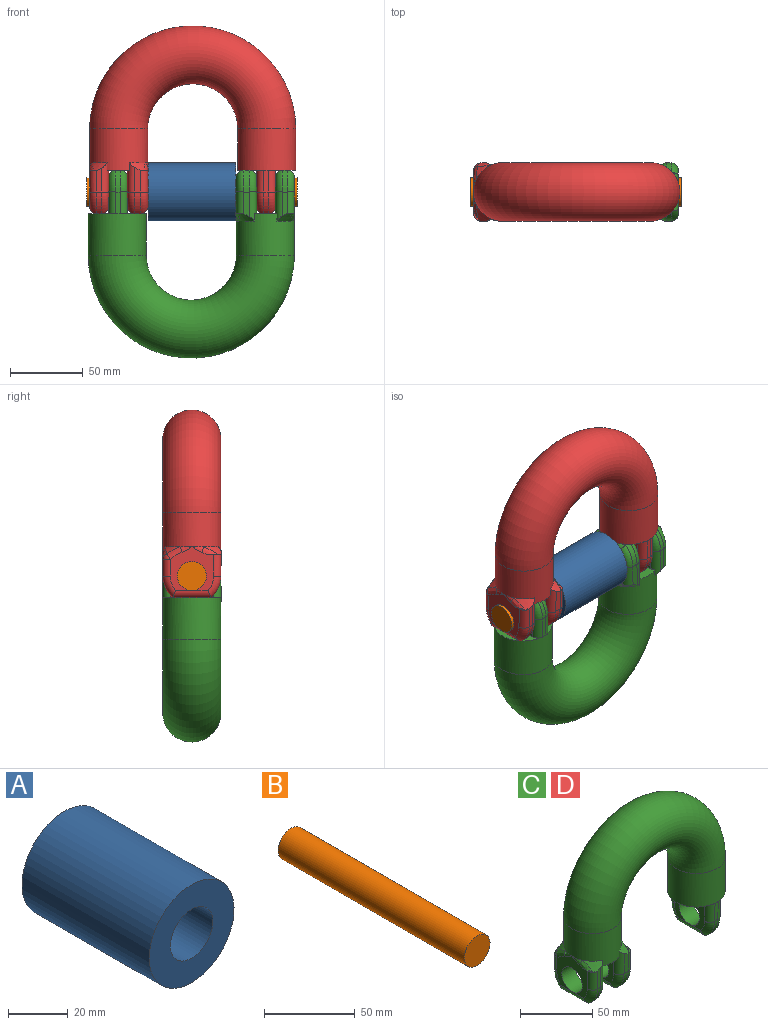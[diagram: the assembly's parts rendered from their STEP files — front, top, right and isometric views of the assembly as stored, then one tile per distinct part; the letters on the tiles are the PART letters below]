
ASSEMBLY  parts=4 mates=3
PART A: 4 faces, bbox 40x60x40 mm
  f0: cylinder r=10mm len=60mm, axis (0,1,0), area 3769.9mm2, adj f2,f3
  f1: cylinder r=20mm len=60mm, axis (0,1,0), area 7539.8mm2, adj f2,f3
  f2: plane 40x40mm, normal (0,-1,0), area 942.5mm2, adj f0,f1
  f3: plane 40x40mm, normal (0,1,0), area 942.5mm2, adj f0,f1
PART B: 3 faces, bbox 20x145x20 mm
  f0: cylinder r=10mm len=145mm, axis (0,1,0), area 9110.6mm2, adj f1,f2
  f1: plane 20x20mm, normal (0,-1,0), area 314.2mm2, adj f0
  f2: plane 20x20mm, normal (0,1,0), area 314.2mm2, adj f0
PART C: 86 faces, bbox 154.5x47.3x137.4 mm
  f0: plane 26.46x3mm, normal (0,0,-1), area 79.4mm2, adj f36,f37,f51,f52
  f1: plane 10.98x5.8mm, normal (0,0,1), area 8.1mm2, adj f10,f42,f63,f85
  f2: plane 24.41x4mm, normal (0,0,-1), area 97.6mm2, adj f29,f65,f69,f70
  f3: plane 7.38x0.67mm, normal (0,0,1), area 1.4mm2, adj f18,f26,f74,f79
  f4: plane 1.99x0.1mm, normal (0,0,1), area 0mm2, adj f18,f27,f76
  f5: plane 26.46x2.99mm, normal (0,0,-1), area 79.1mm2, adj f24,f28,f77,f82
  f6: plane 11.14x6.01mm, normal (0,0,1), area 9mm2, adj f8,f34,f40,f44,f48
  f7: plane 30.16x25mm, normal (1,0,0), area 413mm2, adj f14,f23,f47,f49,f51,f53,f55
  f8: plane 31x30.84mm, normal (-1,0,0), area 452.1mm2, adj f6,f23,f43,f44,f48,f50,f52,f54
  f9: plane 30.16x25mm, normal (-1,0,0), area 413mm2, adj f14,f22,f64,f67,f69,f72,f73
  f10: plane 31x30.84mm, normal (1,0,0), area 460.3mm2, adj f1,f19,f22,f45,f46,f61,f62,f63
  f11: plane 30.16x25mm, normal (1,0,0), area 413mm2, adj f15,f21,f74,f75,f76,f77,f78
  f12: plane 30.16x25mm, normal (-1,0,0), area 413mm2, adj f13,f21,f79,f80,f81,f82,f83
  f13: plane 39.11x16.08mm, normal (0,0,-1), area 359.5mm2, adj f12,f18,f79,f81
  f14: plane 40x15.68mm, normal (0,0,-1), area 517.2mm2, adj f7,f9,f16,f47,f55,f64,f73
  f15: plane 39.7x18.02mm, normal (0,0,-1), area 398.6mm2, adj f11,f18,f74,f76
  f16: cylinder r=20mm len=40mm, axis (0,0,1), area 3112.9mm2, adj f14,f17,f39,f40,f41,f42,f43,f46
  f17: torus R=51mm, axis (0,-1,0), area 20134mm2, adj f16,f18
  f18: cylinder r=20mm len=40mm, axis (0,0,-1), area 3581.4mm2, adj f3,f4,f13,f15,f17,f20
  f19: plane 11.13x6.01mm, normal (0,0,1), area 9mm2, adj f10,f31,f41,f45,f61
  f20: plane 3.92x0.39mm, normal (0,0,1), area 0.3mm2, adj f18,f27,f81
  f21: cylinder r=10mm len=20mm, axis (-1,0,0), area 816.3mm2, adj f11,f12
  f22: cylinder r=10mm len=20mm, axis (-1,0,0), area 879.6mm2, adj f9,f10
  f23: cylinder r=10mm len=20mm, axis (-1,0,0), area 816.8mm2, adj f7,f8
  f24: cylinder r=20mm len=15mm, axis (-1,0,0), area 50.8mm2, adj f5,f25,f74,f75,f79,f80
  f25: plane 3.2x0mm, normal (0,0,-1), area 0mm2, adj f24,f26,f74,f79
  f26: plane 15x2.99mm, normal (0,-1,-0.01), area 44.9mm2, adj f3,f25,f74,f79
  f27: plane 15x2.99mm, normal (0,1,0), area 44.9mm2, adj f4,f20,f28,f76,f81
  f28: cylinder r=20mm len=15mm, axis (-1,0,0), area 50.7mm2, adj f5,f27,f78,f83
  f29: cylinder r=20mm len=15mm, axis (-1,0,0), area 67.9mm2, adj f2,f30,f61,f62,f64,f67
  f30: plane 4.21x0mm, normal (0,0,-1), area 0mm2, adj f29,f31,f61,f64
  f31: plane 17.22x4.21mm, normal (0,-1,-0.01), area 64mm2, adj f19,f30,f41,f61,f64
  f32: plane 17.41x4.23mm, normal (0,1,0), area 64.5mm2, adj f33,f42,f63,f73
  f33: cylinder r=20mm len=13.33mm, axis (-1,0,0), area 58.4mm2, adj f32,f66,f70,f72
  f34: plane 16.64x3.11mm, normal (0,-1,-0.01), area 47.2mm2, adj f6,f35,f40,f47,f48
  f35: plane 3.21x0mm, normal (0,0,-1), area 0mm2, adj f34,f36,f47,f48
  f36: cylinder r=20mm len=15mm, axis (-1,0,0), area 50.9mm2, adj f0,f35,f47,f48,f49,f50
  f37: cylinder r=20mm len=15mm, axis (-1,0,0), area 50.9mm2, adj f0,f38,f53,f54
  f38: plane 13.72x3.01mm, normal (0,1,0), area 38.2mm2, adj f37,f55,f56,f57
  f39: cone r=25mm half-angle=45deg, axis (0,0,-1), area 52.2mm2, adj f16,f57,f59
  f40: cone r=25mm half-angle=45deg, axis (0,0,-1), area 70mm2, adj f6,f16,f34,f44,f47
  f41: cone r=25mm half-angle=45deg, axis (0,0,-1), area 73.1mm2, adj f16,f19,f31,f45,f64
  f42: cone r=25mm half-angle=45deg, axis (0,0,-1), area 71.4mm2, adj f1,f16,f32,f73,f85
  f43: bspline ~9.51x4.04mm, area 10.7mm2, adj f8,f16,f44
  f44: bspline ~13.39x9.91mm, area 33.3mm2, adj f6,f8,f40,f43
  f45: bspline ~13.39x9.91mm, area 33.3mm2, adj f10,f19,f41,f46
  f46: bspline ~9.51x4.04mm, area 10.7mm2, adj f10,f16,f45
  f47: cylinder r=5mm len=20.24mm, axis (0,0.01,-1), area 133.2mm2, adj f7,f14,f16,f34,f35,f36,f40,f49
  f48: cylinder r=5mm len=15.26mm, axis (0,0.01,-1), area 119.3mm2, adj f6,f8,f34,f35,f36,f50
  f49: torus R=15mm, axis (-1,0,0), area 111.6mm2, adj f7,f36,f47,f51
  f50: torus R=15mm, axis (1,0,0), area 111.6mm2, adj f8,f36,f48,f52
  f51: cylinder r=5mm len=26.46mm, axis (0,-1,0), area 191.7mm2, adj f0,f7,f49,f53
  f52: cylinder r=5mm len=26.46mm, axis (0,-1,0), area 191.7mm2, adj f0,f8,f50,f54
  f53: torus R=15mm, axis (-1,0,0), area 113.1mm2, adj f7,f37,f51,f55
  f54: torus R=15mm, axis (1,0,0), area 113.1mm2, adj f8,f37,f52,f56
  f55: cylinder r=5mm len=20mm, axis (0,0,1), area 125.9mm2, adj f7,f14,f16,f38,f53,f57
  f56: cylinder r=5mm len=11.72mm, axis (0,0,1), area 92mm2, adj f8,f38,f54,f58
  f57: bspline ~14.17x10.45mm, area 36.5mm2, adj f16,f38,f39,f55,f58
  f58: sphere r=5mm, area 14.6mm2, adj f56,f57,f59
  f59: bspline ~13.39x9.91mm, area 48.1mm2, adj f8,f39,f58,f60
  f60: bspline ~9.51x4.04mm, area 10.7mm2, adj f8,f16,f59
  f61: cylinder r=5mm len=15.26mm, axis (0,0.01,-1), area 119.3mm2, adj f10,f19,f29,f30,f31,f62
  f62: torus R=15mm, axis (1,0,0), area 111.6mm2, adj f10,f29,f61,f65
  f63: cylinder r=5mm len=15mm, axis (0,0,1), area 117.8mm2, adj f1,f10,f32,f66
  f64: cylinder r=5mm len=20.25mm, axis (0,-0.01,1), area 133mm2, adj f9,f14,f16,f29,f30,f31,f41,f67
  f65: cylinder r=5mm len=24.41mm, axis (0,-1,0), area 183.7mm2, adj f2,f10,f62,f68
  f66: torus R=15mm, axis (1,0,0), area 104.2mm2, adj f10,f33,f63,f68
  f67: torus R=15mm, axis (-1,0,0), area 111.6mm2, adj f9,f29,f64,f69
  f68: sphere r=5mm, area 16.6mm2, adj f65,f66,f70
  f69: cylinder r=5mm len=24.41mm, axis (0,-1,0), area 183.7mm2, adj f2,f9,f67,f71
  f70: cylinder r=5mm len=4mm, axis (-1,0,0), area 16.8mm2, adj f2,f33,f68,f71
  f71: sphere r=5mm, area 30mm2, adj f69,f70,f72
  f72: torus R=15mm, axis (-1,0,0), area 104.2mm2, adj f9,f33,f71,f73
  f73: cylinder r=5mm len=20mm, axis (0,0,-1), area 131.8mm2, adj f9,f14,f16,f32,f42,f72
  f74: cylinder r=5mm len=15.26mm, axis (0,0.01,-1), area 119.3mm2, adj f3,f11,f15,f24,f25,f26,f75
  f75: torus R=15mm, axis (-1,0,0), area 111.6mm2, adj f11,f24,f74,f77
  f76: cylinder r=5mm len=15mm, axis (0,0,1), area 117.8mm2, adj f4,f11,f15,f27,f78
  f77: cylinder r=5mm len=26.46mm, axis (0,-1,0), area 191.7mm2, adj f5,f11,f75,f78
  f78: torus R=15mm, axis (-1,0,0), area 113.1mm2, adj f11,f28,f76,f77
  f79: cylinder r=5mm len=15.26mm, axis (0,-0.01,1), area 119.3mm2, adj f3,f12,f13,f24,f25,f26,f80
  f80: torus R=15mm, axis (-1,0,0), area 111.6mm2, adj f12,f24,f79,f82
  f81: cylinder r=5mm len=15mm, axis (0,0,-1), area 117.8mm2, adj f12,f13,f20,f27,f83
  f82: cylinder r=5mm len=26.46mm, axis (0,1,0), area 191.7mm2, adj f5,f12,f80,f83
  f83: torus R=15mm, axis (-1,0,0), area 113.1mm2, adj f12,f28,f81,f82
  f84: bspline ~9.51x4.04mm, area 10.7mm2, adj f10,f16,f85
  f85: bspline ~13.39x9.91mm, area 33.3mm2, adj f1,f10,f42,f84
PART D: same geometry as C
PLACE A rot(axis=(0.71,-0.71,0),180deg) t=(-8.35,7.57,-31.78)mm
PLACE B rot(axis=(0,0,1),90deg) t=(-8.35,7.57,-31.78)mm
PLACE C rot(axis=(0,-1,0),180deg) t=(-8.85,7.57,-75.28)mm
PLACE D t=(-7.86,7.57,11.72)mm
MATE fastened B.f0 <-> C.f21  axis (1,0,0) through (64.15,7.57,-31.78)mm
MATE fastened A.f0 <-> B.f0  axis (-1,0,0) through (-8.35,7.57,-31.78)mm
MATE fastened C.f21 <-> D.f21  axis (1,0,0) through (36.15,7.57,-31.78)mm
